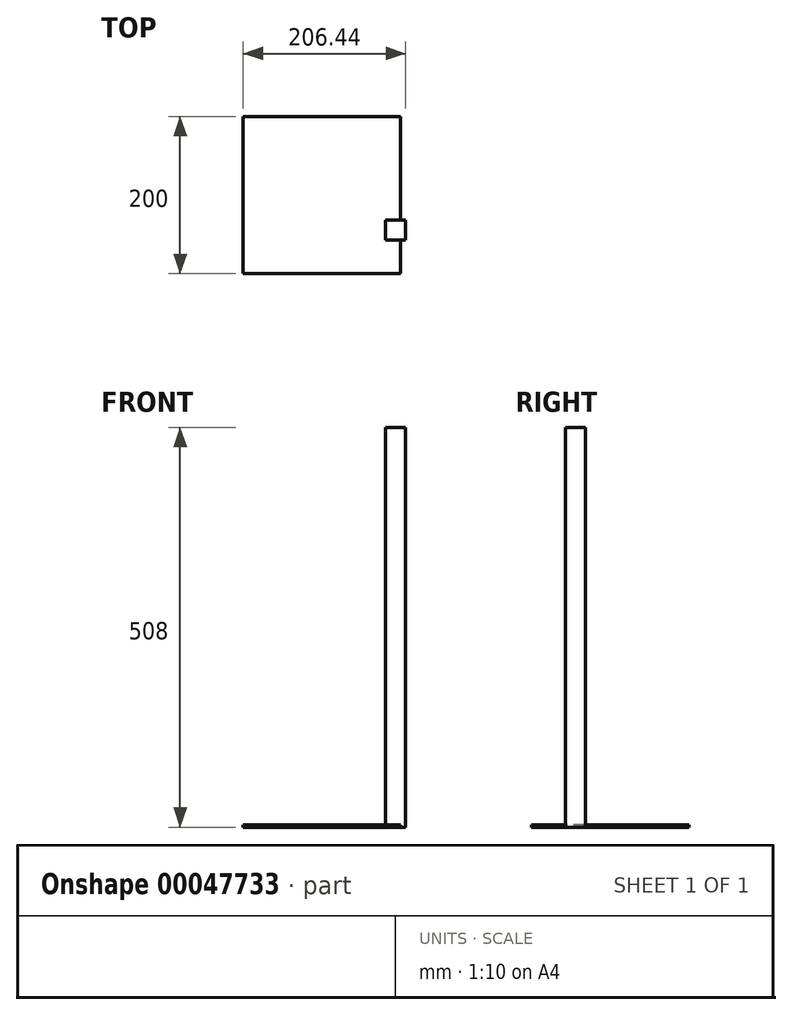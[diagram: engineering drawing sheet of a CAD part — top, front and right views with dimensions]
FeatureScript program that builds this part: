
annotation { "Feature Type Name" : "Feature", "Feature Type Description" : "" }
export const myFeature = defineFeature(function(context is Context, id is Id, definition is map)
    precondition{}
    {
        {
            var Q0;
            Q0=qCreatedBy(makeId("Top.planeOp"),FACE);
            var sketch = newSketch(context, id + "F0", { "sketchPlane" : qUnion([Q0])});
            skLineSegment(sketch, "E0.bottom", {"start": v(-12.16, 15.33) * mm, "end": v(13.24, 15.33) * mm});
            skLineSegment(sketch, "E0.top", {"start": v(-12.16, -10.07) * mm, "end": v(13.24, -10.07) * mm});
            skLineSegment(sketch, "E0.left", {"start": v(-12.16, 15.33) * mm, "end": v(-12.16, -10.07) * mm});
            skLineSegment(sketch, "E0.right", {"start": v(13.24, 15.33) * mm, "end": v(13.24, -10.07) * mm});
            skSolve(sketch);
        }
        {
            var Q0;
            Q0=makeQuery(id+"F0.imprint","IMPRINT",FACE,{"disambiguationData":[TD([[makeQuery(id+"F0.imprint","IMPRINT",EDGE,{"derivedFrom":sQuery(id+"F0.wireOp",EDGE,"E0.bottom")}),-1.0]])]});
            extrude(context, id + "F1", {"entities" : qUnion([Q0]), "depth" : 508 * mm});
        }
        {
            var Q0;
            Q0=makeQuery(id+"F0.imprint","IMPRINT",FACE,{"disambiguationData":[TD([[makeQuery(id+"F0.imprint","IMPRINT",EDGE,{"derivedFrom":sQuery(id+"F0.wireOp",EDGE,"E0.bottom")}),-1.0]])]});
            extrude(context, id + "F2", {"entities" : qUnion([Q0]), "operationType" : NewBodyOperationType.ADD, "depth" : 355.6 * mm});
        }
        {
            var Q0;
            Q0=qCreatedBy(makeId("Top.planeOp"),FACE);
            var sketch = newSketch(context, id + "F3", { "sketchPlane" : qUnion([Q0])});
            skLineSegment(sketch, "E1.bottom", {"start": v(-193.2, 147.16) * mm, "end": v(6.8, 147.16) * mm});
            skLineSegment(sketch, "E1.top", {"start": v(-193.2, -52.84) * mm, "end": v(6.8, -52.84) * mm});
            skLineSegment(sketch, "E1.left", {"start": v(-193.2, 147.16) * mm, "end": v(-193.2, -52.84) * mm});
            skLineSegment(sketch, "E1.right", {"start": v(6.8, 147.16) * mm, "end": v(6.8, -52.84) * mm});
            skSolve(sketch);
        }
        {
            var Q0;
            Q0 = qSketchRegion(id + "F3", true);
            extrude(context, id + "F4", {"entities" : qUnion([Q0]), "operationType" : NewBodyOperationType.ADD, "depth" : 3.17 * mm});
        }
    });
